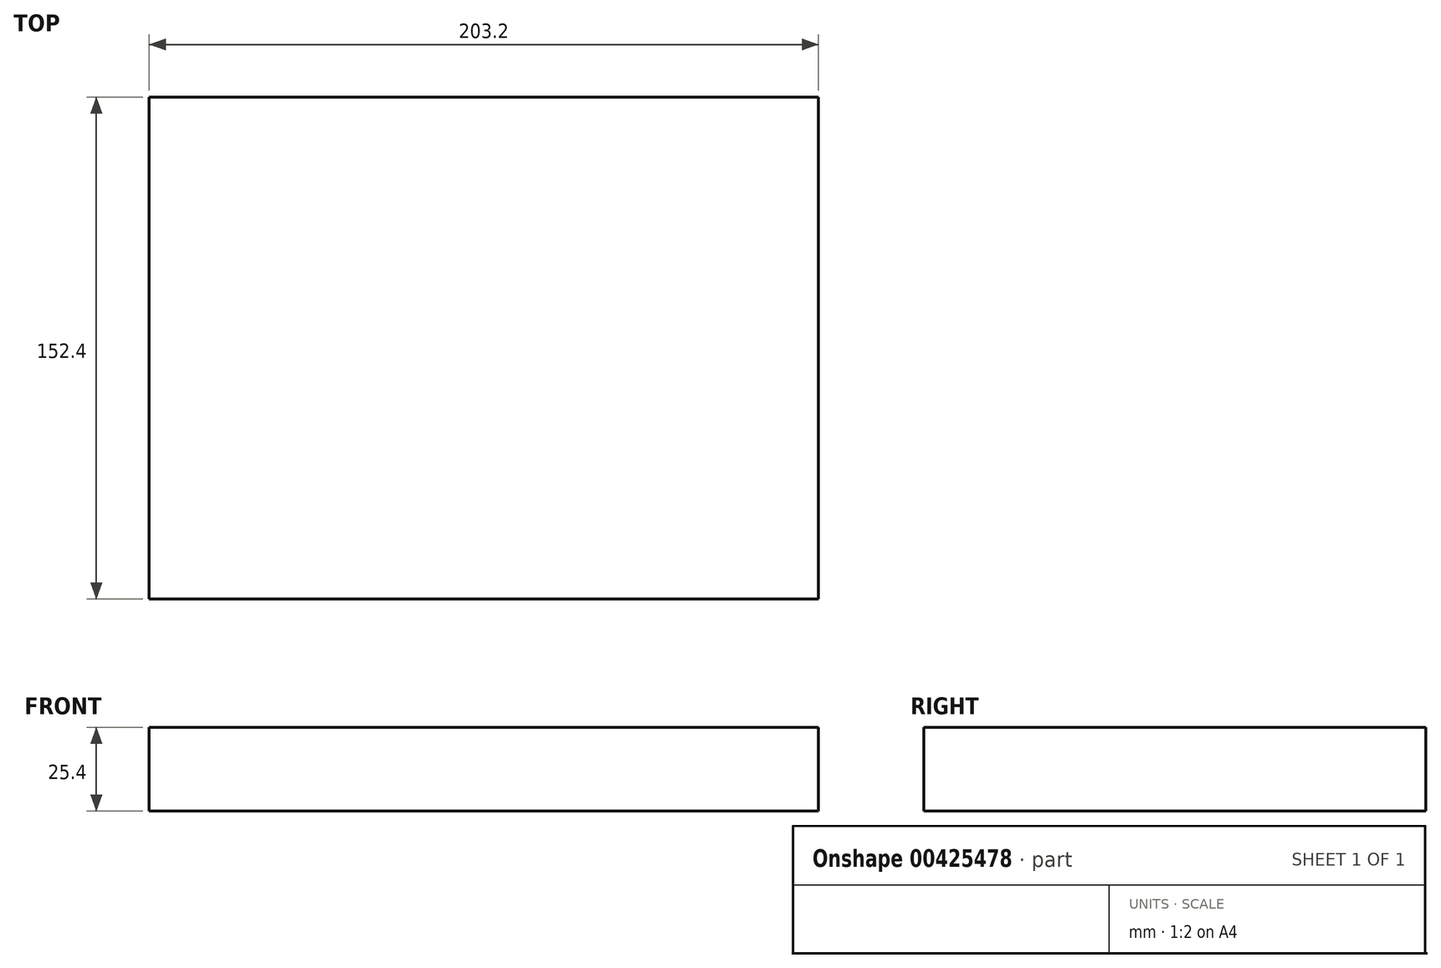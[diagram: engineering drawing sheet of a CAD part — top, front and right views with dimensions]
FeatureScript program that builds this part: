
annotation { "Feature Type Name" : "Feature", "Feature Type Description" : "" }
export const myFeature = defineFeature(function(context is Context, id is Id, definition is map)
    precondition{}
    {
        {
            var Q0;
            Q0=qCreatedBy(makeId("Top.planeOp"),FACE);
            var sketch = newSketch(context, id + "F0", { "sketchPlane" : qUnion([Q0])});
            skLineSegment(sketch, "E0.bottom", {"start": v(101.6, 76.2) * mm, "end": v(-101.6, 76.2) * mm});
            skLineSegment(sketch, "E0.top", {"start": v(101.6, -76.2) * mm, "end": v(-101.6, -76.2) * mm});
            skLineSegment(sketch, "E0.left", {"start": v(101.6, 76.2) * mm, "end": v(101.6, -76.2) * mm});
            skLineSegment(sketch, "E0.right", {"start": v(-101.6, 76.2) * mm, "end": v(-101.6, -76.2) * mm});
            skPoint(sketch, "E0.middle", {"position": v(0, 0) * mm});
            skSolve(sketch);
        }
        {
            var Q0;
            Q0=makeQuery(id+"F0.imprint","IMPRINT",FACE,{"disambiguationData":[TD([[makeQuery(id+"F0.imprint","IMPRINT",EDGE,{"derivedFrom":sQuery(id+"F0.wireOp",EDGE,"E0.bottom")}),1.0]])]});
            extrude(context, id + "F1", {"entities" : qUnion([Q0]), "depth" : 25.4 * mm});
        }
    });
